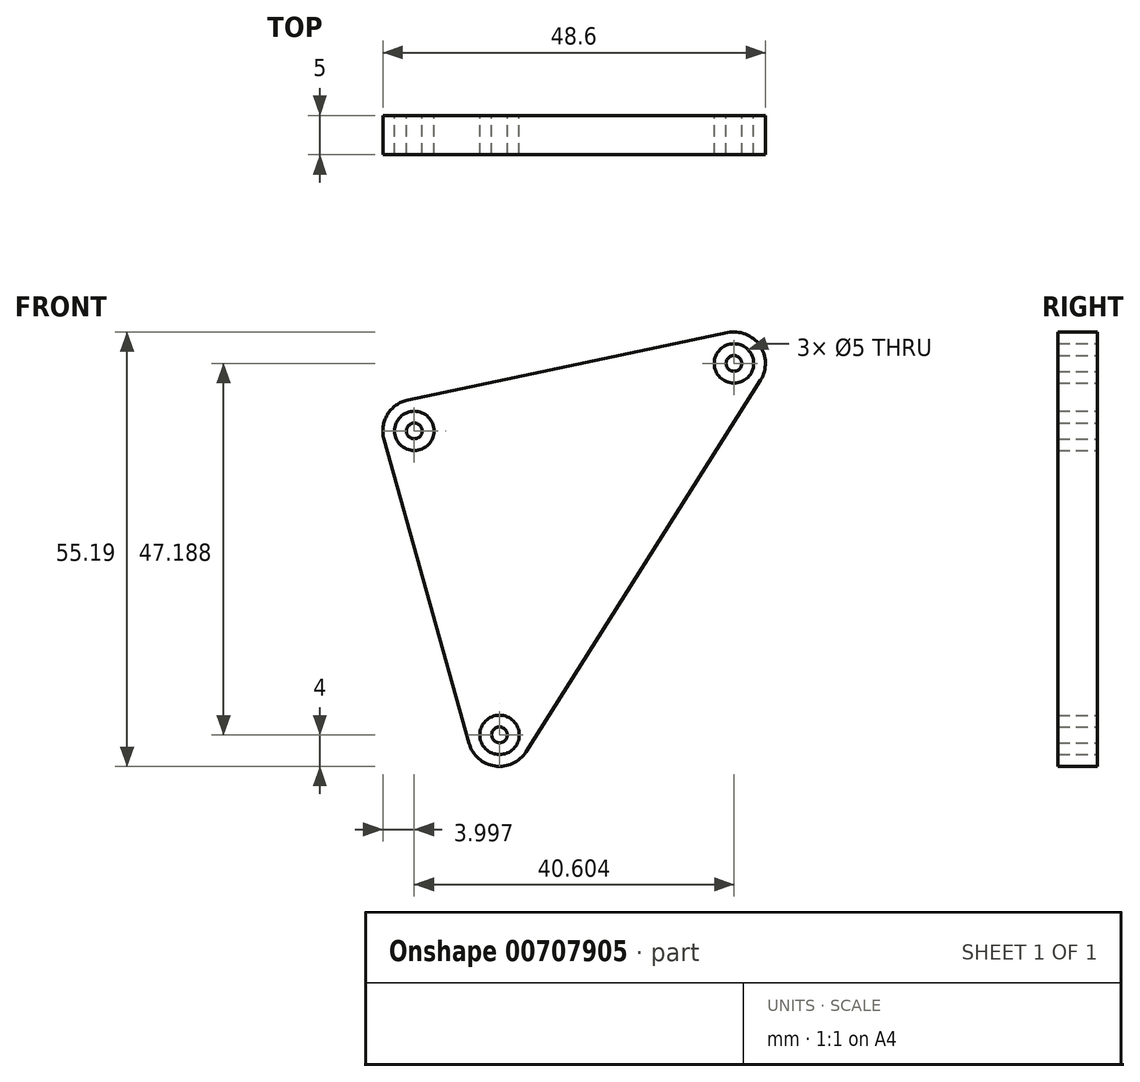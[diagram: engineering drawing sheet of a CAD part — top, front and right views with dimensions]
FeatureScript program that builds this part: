
annotation { "Feature Type Name" : "Feature", "Feature Type Description" : "" }
export const myFeature = defineFeature(function(context is Context, id is Id, definition is map)
    precondition{}
    {
        {
            var Q0;
            Q0=qCreatedBy(makeId("Front.planeOp"),FACE);
            var sketch = newSketch(context, id + "F0", { "sketchPlane" : qUnion([Q0])});
            skLineSegment(sketch, "E0", {"start": v(0, 0) * mm, "end": v(-10.82, 38.61) * mm, "construction": true});
            skLineSegment(sketch, "E1", {"start": v(-10.82, 38.61) * mm, "end": v(29.78, 47.19) * mm, "construction": true});
            skLineSegment(sketch, "E2", {"start": v(29.78, 47.19) * mm, "end": v(0, 0) * mm, "construction": true});
            skCircle(sketch, "E3", {"center": v(0, 0) * mm, "radius": 1 * mm});
            skCircle(sketch, "E4", {"center": v(0, 0) * mm, "radius": 2.5 * mm});
            skArc(sketch, "E5", {"start": v(-3.85, -1.08) * mm, "mid": v(-0.58, -3.96) * mm, "end": v(3.38, -2.13) * mm});
            skCircle(sketch, "E6", {"center": v(-10.82, 38.61) * mm, "radius": 1 * mm});
            skCircle(sketch, "E7", {"center": v(-10.82, 38.61) * mm, "radius": 2.5 * mm});
            skArc(sketch, "E8", {"start": v(-11.65, 42.53) * mm, "mid": v(-14.24, 40.68) * mm, "end": v(-14.67, 37.53) * mm});
            skCircle(sketch, "E9", {"center": v(29.78, 47.19) * mm, "radius": 1 * mm});
            skArc(sketch, "E10", {"start": v(33.16, 45.05) * mm, "mid": v(33.06, 49.47) * mm, "end": v(28.95, 51.1) * mm});
            skCircle(sketch, "E11", {"center": v(29.78, 47.19) * mm, "radius": 2.5 * mm});
            skLineSegment(sketch, "E12", {"start": v(-3.85, -1.08) * mm, "end": v(-14.67, 37.53) * mm});
            skLineSegment(sketch, "E13", {"start": v(-11.65, 42.53) * mm, "end": v(28.95, 51.1) * mm});
            skLineSegment(sketch, "E14", {"start": v(33.16, 45.05) * mm, "end": v(3.38, -2.13) * mm});
            skSolve(sketch);
        }
        {
            var Q0;
            Q0=makeQuery(id+"F0.imprint","IMPRINT",FACE,{"disambiguationData":[TD([[makeQuery(id+"F0.imprint","IMPRINT",EDGE,{"derivedFrom":sQuery(id+"F0.wireOp",EDGE,"E6")}),1.0]])]});
            var Q1;
            Q1=makeQuery(id+"F0.imprint","IMPRINT",FACE,{"disambiguationData":[TD([[makeQuery(id+"F0.imprint","IMPRINT",EDGE,{"derivedFrom":sQuery(id+"F0.wireOp",EDGE,"E4")}),-1.0]])]});
            var Q2;
            Q2=makeQuery(id+"F0.imprint","IMPRINT",FACE,{"disambiguationData":[TD([[makeQuery(id+"F0.imprint","IMPRINT",EDGE,{"derivedFrom":sQuery(id+"F0.wireOp",EDGE,"E9")}),1.0]])]});
            var Q3;
            Q3=makeQuery(id+"F0.imprint","IMPRINT",FACE,{"disambiguationData":[TD([[makeQuery(id+"F0.imprint","IMPRINT",EDGE,{"derivedFrom":sQuery(id+"F0.wireOp",EDGE,"E3")}),1.0]])]});
            extrude(context, id + "F1", {"entities" : qUnion([Q0, Q1, Q2, Q3]), "depth" : 5 * mm, "offsetDistance" : 25.4 * mm});
        }
    });
